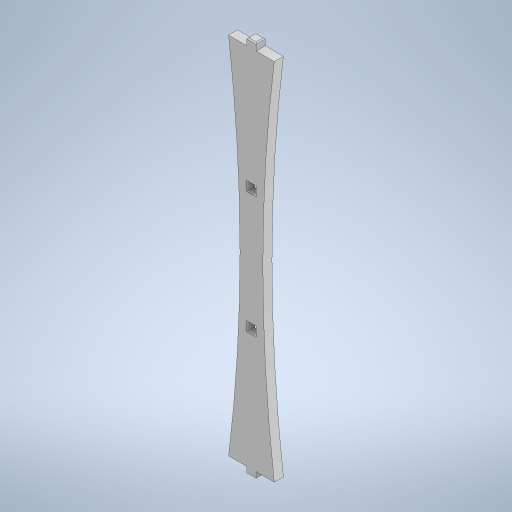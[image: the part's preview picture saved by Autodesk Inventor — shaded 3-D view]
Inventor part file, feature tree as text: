
AUTODESK INVENTOR PART (.ipt)
format: ipt  version: 2024 (Build 280153000, 153)  size: 304,128 bytes
history: native  units: in
note: dims shown in document units (in); Inventor stores cm internally (conversion verified against a paired STEP export)
features: chamfer x2, extrude x1, sketch x1
ambient origin geometry x8: Origin, YZ Plane, XZ Plane, XY Plane, X Axis, Y Axis, Z Axis, Center Point
bodies: Solid1 (feature_tree)
feature tree (4):
  extrude  "Extrusion1"  Depth=6.5256in
  chamfer  "Chamfer1"  Distance=0.1575in
  chamfer  "Chamfer2"  Distance=0.1614in
  sketch  "Sketch1"  dims[d0=0.3937in d1=6.5256in d2=0.1575in d3=0.0in d4=0.1614in d5=0.1614in d6=1.935in d7=0.1614in d8=0.1614in d9=0.1969in d10=0.1181in d11=0.1181in d12=0.0197in d13=0.0787in d14=45.0deg d15=0.0295in d16=0.0787in d17=45.0deg d18=0.1969in d19=0.1969in d20=0.1969in d21=0.1969in]
